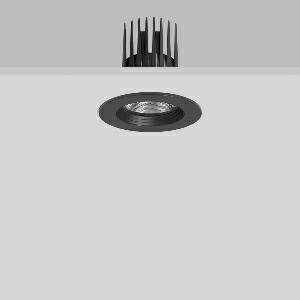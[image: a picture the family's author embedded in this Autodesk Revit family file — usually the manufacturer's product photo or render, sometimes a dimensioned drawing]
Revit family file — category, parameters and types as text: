
# Revit family: heledon_mini_e_901748_003_3_76_3fbe
name_source: partatom
category: Lighting Fixtures
units: mm (PartAtom-declared; Revit-internal decimal feet)

## family parameters
Cut with Voids When Loaded = No
Host = Face
Light Source = No
Part Type = Normal
Room Calculation Point = No
Round Connector Dimension = Use Diameter
Shared = No

## types (1)
- HELEDON mini E (1 x LED Modul 935, 3700 lm, 3500)
    Apparent Load = 29 VA
    Approval mark = CE
    CIE Flux Codes = 100 100 100 100 100
    Color Rendering = 92
    Color Temperature = 3500
    Default Elevation = 1800 mm
    Description = Series: HELEDON mini
Round recessed downlight. Housing: die-cast aluminium, powder-coated. Black plastic ring and recessed LED to prevent glare from the side. Optical assembly with reflector made of MIRO-Silver with 98% total light reflection for outstanding efficiency - can be changed without tools. Best colour rendering index Ra>90. Suitable for Recessed ceiling mounting. Installation without tools thanks to spring fastening system. Including separate LED converter with connecting cable 600 mm.High quality converter without flickering and stroboscopic effect. Through-wiring box (5 pole) available as accessory. The following accessories can be mounted without use of tools: interchangeable lenses, decorative glasses, honeycomb louvre, clear and frosted diffusers, white interchangeable plastic ring. 
Colour: deep black, matt (RAL 9005)
Diameter: 124 mm
Height: 3 mm
Cut-out diameter: 114 mm
Recess height: 170 mm
Luminaire: recess height: 120 mm
Lamp: LED
Socket: without socket
Colour temperature: 3500K
Colour rendering index (CRI): 92
System power: 29 W
Rated luminous flux: 3700 lm
Luminous efficiency: 128 lm/W
Control gear: Converter, dimmable, DALI
Protection class: II
Type of protection: IP 20
    Height = 0 mm  [stored 0 ft]
    Lamp = 1 x LED Modul 935
    Lamp Light Flux = 3700 lm
    Lamp count = 1
    Length = 124 mm  [stored 0.406824 ft]
    Lifetime = 50000 h
    Luminous efficacy = 128 lm/W
    Manufacturer = RZB
    ModVariant = No
    Model = 901748.003.3.76
    Mounting Place = Ceiling
    Mounting Type = Recessed
    Number of Poles = 1
    OnlyDefault = Yes
    Power Factor = 1
    Product Name = HELEDON mini E
    Product group = Recessed downlights
    ProductGroupID = 402
    Protection Class = Protection class II
    Protection Degree = IP 20
    RLX_Detail_Level = 1
    RLX_Emergency_Light_Flux = 0 lm
    RLX_Emergency_Type = 0
    RLX_Emergency_Type_DB = No
    RlxData = <blob elided: 126189 chars, md5=aa104127>
    Socket = socket
    Standby Power = 0 W
    System Light Flux = 3700 lm
    System Power = 29 W
    Type Comments = Product without accessories
    Type Image = 901657.003.jpg
    URL = http://relux.com
    VarID = ---
    Voltage = 230 V
    Voltage Range = 220-240 V
    Weight = 0.00 kg
    Width = 0 mm  [stored 0 ft]

note: [stored X ft] marks values corroborated as IEEE doubles in the binary element streams (Revit-internal decimal feet)

## geometry (parser evidence)
native form markers: Blend x4, Sweep x12
no freeform markers — native parametric forms only
